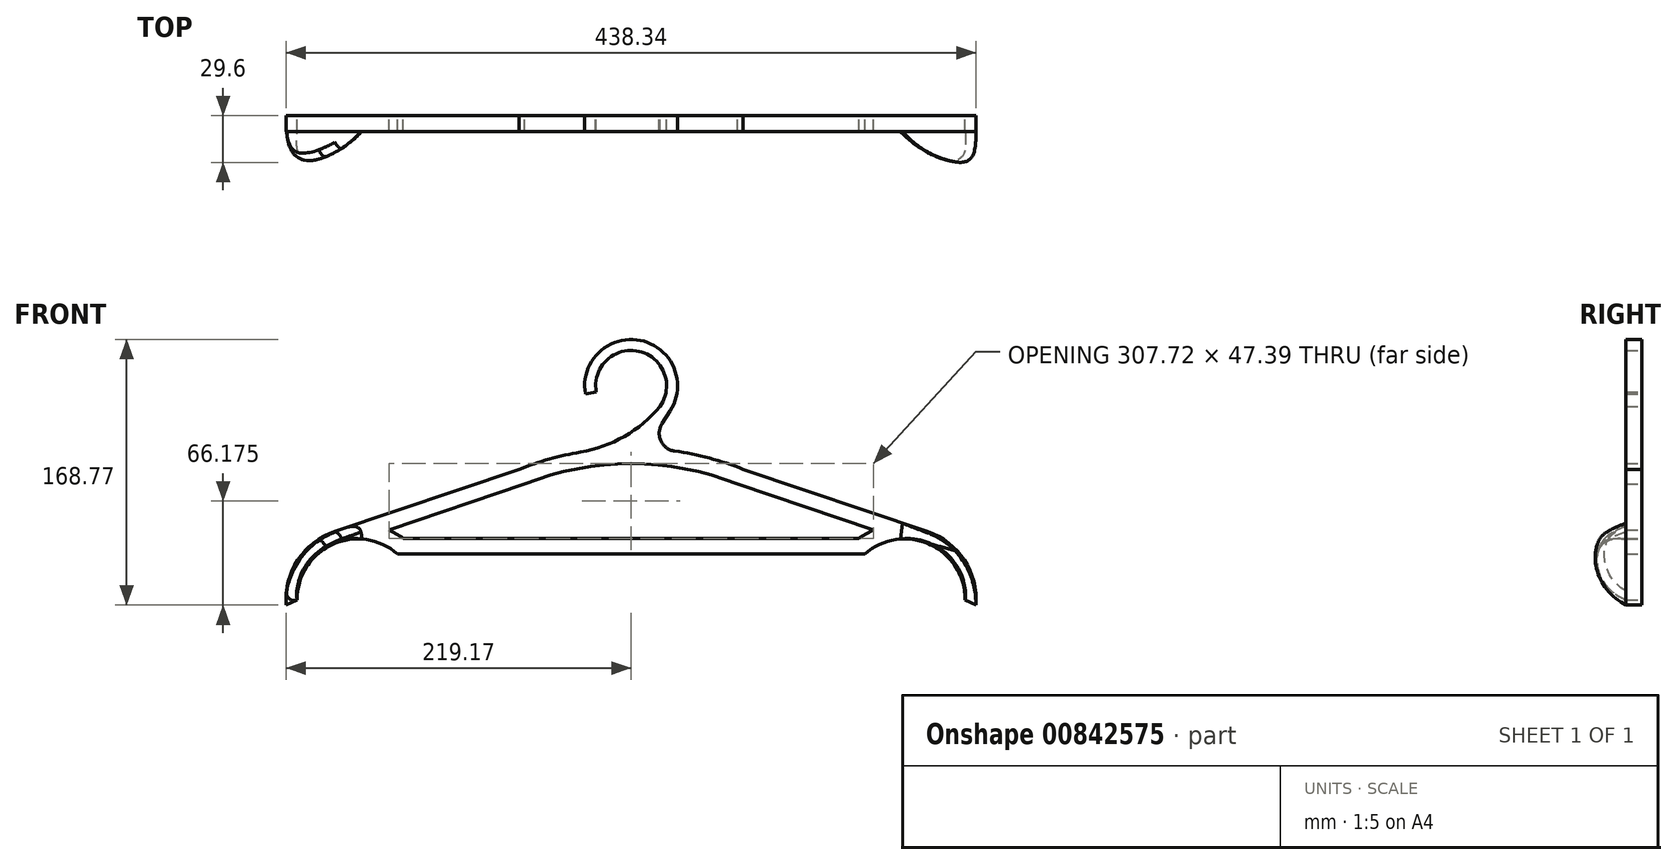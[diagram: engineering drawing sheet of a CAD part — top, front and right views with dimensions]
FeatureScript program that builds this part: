
annotation { "Feature Type Name" : "Feature", "Feature Type Description" : "" }
export const myFeature = defineFeature(function(context is Context, id is Id, definition is map)
    precondition{}
    {
        {
            var Q0;
            Q0=qCreatedBy(makeId("Front.planeOp"),FACE);
            var sketch = newSketch(context, id + "F0", { "sketchPlane" : qUnion([Q0])});
            skLineSegment(sketch, "E0.top", {"start": v(212.5, 102.5) * mm, "end": v(-212.5, 102.5) * mm, "construction": true});
            skPoint(sketch, "E0.middle", {"position": v(0, 0) * mm});
            skLineSegment(sketch, "E1", {"start": v(0, -35.02) * mm, "end": v(0, 25.02) * mm, "construction": true});
            skArc(sketch, "E2", {"start": v(-188.33, -20.83) * mm, "mid": v(-211.7, -38.89) * mm, "end": v(-219.02, -67.5) * mm});
            skArc(sketch, "E3", {"start": v(24.82, 55.82) * mm, "mid": v(5.78, 100.7) * mm, "end": v(-29.04, 66.58) * mm});
            skArc(sketch, "E4.0", {"start": v(15.87, 55.82) * mm, "mid": v(6.77, 93.23) * mm, "end": v(-22.15, 67.81) * mm});
            skArc(sketch, "E5.0", {"start": v(148.4, -35.02) * mm, "mid": v(189.72, -28.9) * mm, "end": v(212.17, -64.13) * mm});
            skArc(sketch, "E6.0", {"start": v(-148.4, -35.02) * mm, "mid": v(-189.72, -28.9) * mm, "end": v(-212.17, -64.13) * mm});
            skLineSegment(sketch, "E7", {"start": v(173.49, -109.23) * mm, "end": v(174.07, -109.23) * mm});
            skLineSegment(sketch, "E8.MirrorCS", {"start": v(71.13, 18.83) * mm, "end": v(188.33, -20.83) * mm});
            skPoint(sketch, "E9.start.orphan", {"position": v(-188.33, -28.3) * mm});
            skPoint(sketch, "E10.orphan", {"position": v(-173.49, -102.23) * mm});
            skLineSegment(sketch, "E11.trimOffspring", {"start": v(173.78, -102.23) * mm, "end": v(174.07, -102.23) * mm});
            skArc(sketch, "E12.trimOffspring", {"start": v(188.33, -20.83) * mm, "mid": v(211.7, -38.89) * mm, "end": v(219.02, -67.5) * mm});
            skPoint(sketch, "E13.MirrorCS.start.orphan", {"position": v(188.33, -28.3) * mm});
            skLineSegment(sketch, "E14.trimOffspring", {"start": v(212.5, -40.14) * mm, "end": v(212.5, 102.5) * mm, "construction": true});
            skPoint(sketch, "E0.bottom.start.orphan", {"position": v(212.5, -102.5) * mm});
            skLineSegment(sketch, "E15", {"start": v(-4.97, 25.02) * mm, "end": v(-4.97, 24.95) * mm, "construction": true});
            skLineSegment(sketch, "E16", {"start": v(5.03, 24.95) * mm, "end": v(5.03, 25.02) * mm, "construction": true});
            skLineSegment(sketch, "E17", {"start": v(9.6, 32.13) * mm, "end": v(24.82, 55.82) * mm});
            skLineSegment(sketch, "E18", {"start": v(0, 32.37) * mm, "end": v(7.33, 43.2) * mm});
            skLineSegment(sketch, "E19", {"start": v(-22.15, 67.81) * mm, "end": v(-29.04, 66.58) * mm});
            skPoint(sketch, "E20.third.point", {"position": v(0, 32.37) * mm});
            skLineSegment(sketch, "E21.trimOffspring", {"start": v(-71.13, 18.83) * mm, "end": v(-188.33, -20.83) * mm});
            skPoint(sketch, "E22.orphan", {"position": v(-52.84, 25.02) * mm});
            skArc(sketch, "E23.trimOffspring", {"start": v(0, 32.37) * mm, "mid": v(-36.2, 28.95) * mm, "end": v(-71.13, 18.83) * mm});
            skPoint(sketch, "E24.orphan", {"position": v(15.87, 55.82) * mm});
            skLineSegment(sketch, "E25", {"start": v(7.33, 43.2) * mm, "end": v(15.87, 55.82) * mm});
            skArc(sketch, "E26.trimOffspring", {"start": v(71.13, 18.83) * mm, "mid": v(40.9, 28) * mm, "end": v(9.6, 32.13) * mm});
            skPoint(sketch, "E27.start.orphan", {"position": v(0, 25.02) * mm});
            skPoint(sketch, "E28.right.start.orphan", {"position": v(-52.84, 17.55) * mm});
            skPoint(sketch, "E29.orphan", {"position": v(52.84, 25.02) * mm});
            skPoint(sketch, "E30.orphan", {"position": v(52.84, 17.55) * mm});
            skLineSegment(sketch, "E31.0", {"start": v(-52.84, -35.02) * mm, "end": v(-138.7, -35.02) * mm});
            skLineSegment(sketch, "E31.1", {"start": v(52.84, -35.02) * mm, "end": v(-52.84, -35.02) * mm});
            skLineSegment(sketch, "E31.2", {"start": v(52.84, -35.02) * mm, "end": v(138.7, -35.02) * mm});
            skLineSegment(sketch, "E32", {"start": v(-138.7, -35.02) * mm, "end": v(-148.4, -35.02) * mm});
            skLineSegment(sketch, "E33", {"start": v(-212.17, -64.13) * mm, "end": v(-219.02, -67.5) * mm});
            skLineSegment(sketch, "E34.MirrorCS", {"start": v(212.17, -64.13) * mm, "end": v(219.02, -67.5) * mm});
            skLineSegment(sketch, "E35.MirrorCS", {"start": v(138.7, -35.02) * mm, "end": v(148.4, -35.02) * mm});
            skPoint(sketch, "E36.orphan", {"position": v(-241.12, -78.36) * mm});
            skPoint(sketch, "E37.orphan", {"position": v(-173.49, -109.23) * mm});
            skPoint(sketch, "E38.orphan", {"position": v(-152.98, -35.02) * mm});
            skArc(sketch, "E39.trimOffspring", {"start": v(174.07, -109.23) * mm, "mid": v(173.78, -109.23) * mm, "end": v(173.49, -109.23) * mm});
            skPoint(sketch, "E40.orphan", {"position": v(152.98, -35.02) * mm});
            skPoint(sketch, "E41.orphan", {"position": v(241.12, -78.36) * mm});
            skPoint(sketch, "E42.orphan", {"position": v(0, -102.5) * mm});
            skPoint(sketch, "E28.top.start.orphan", {"position": v(52.84, -25.02) * mm});
            skPoint(sketch, "E43.trimOffspring.start.orphan", {"position": v(150.24, -25.02) * mm});
            skPoint(sketch, "E44.start.orphan", {"position": v(-52.84, -25.02) * mm});
            skPoint(sketch, "E45.trimOffspring.start.orphan", {"position": v(-150.24, -25.02) * mm});
            skLineSegment(sketch, "E46.trimOffspring", {"start": v(0, 32.37) * mm, "end": v(0, 102.5) * mm, "construction": true});
            skPoint(sketch, "E47.visualSharp", {"position": v(163, -19.73) * mm});
            skPoint(sketch, "E48.visualSharp", {"position": v(-163, -19.73) * mm});
            skLineSegment(sketch, "E49.0", {"start": v(52.84, -25.02) * mm, "end": v(-52.84, -25.02) * mm});
            skLineSegment(sketch, "E49.1", {"start": v(52.84, -25.02) * mm, "end": v(138.7, -25.02) * mm});
            skLineSegment(sketch, "E49.2", {"start": v(138.7, -25.02) * mm, "end": v(144.87, -25.02) * mm});
            skArc(sketch, "E49.3", {"start": v(144.87, -25.02) * mm, "mid": v(149.22, -22.13) * mm, "end": v(153.86, -19.73) * mm});
            skLineSegment(sketch, "E49.4", {"start": v(67.68, 9.44) * mm, "end": v(153.86, -19.73) * mm});
            skLineSegment(sketch, "E49.5", {"start": v(-52.84, -25.02) * mm, "end": v(-138.7, -25.02) * mm});
            skLineSegment(sketch, "E49.6", {"start": v(-138.7, -25.02) * mm, "end": v(-144.87, -25.02) * mm});
            skArc(sketch, "E49.7", {"start": v(-144.87, -25.02) * mm, "mid": v(-149.22, -22.13) * mm, "end": v(-153.86, -19.73) * mm});
            skLineSegment(sketch, "E49.8", {"start": v(-67.68, 9.44) * mm, "end": v(-153.86, -19.73) * mm});
            skArc(sketch, "E49.9", {"start": v(-8.7, 22.16) * mm, "mid": v(-38.72, 18.24) * mm, "end": v(-67.68, 9.44) * mm});
            skArc(sketch, "E49.10", {"start": v(67.68, 9.44) * mm, "mid": v(30.17, 19.87) * mm, "end": v(-8.7, 22.16) * mm});
            skPoint(sketch, "E50.orphan", {"position": v(-212.5, -102.5) * mm});
            skSolve(sketch);
        }
        {
            var Q0;
            {var subQ6=sQuery(id+"F0.wireOp",EDGE,"E2");Q0=makeQuery(id+"F0.imprint","IMPRINT",FACE,{"disambiguationData":[TD([[makeQuery(id+"F0.imprint","IMPRINT",EDGE,{"derivedFrom":subQ6}),1.0]])]});}
            extrude(context, id + "F1", {"entities" : qUnion([Q0]), "depth" : 10 * mm, "offsetDistance" : 25 * mm});
        }
        {
            var Q0;
            Q0=makeQuery(id+"F1.opExtrude","SWEPT_EDGE",EDGE,{"disambiguationData":[OSD([sQuery(id+"F0.wireOp",EDGE,"E4.0"),sQuery(id+"F0.wireOp",EDGE,"E25")])]});
            fillet(context, id + "F2", {"entities" : qUnion([Q0]), "radius" : 1373.13 * mm, "tangentPropagation" : true, "allowEdgeOverflow" : false});
        }
        {
            var Q0;
            Q0=makeQuery(id+"F1.opExtrude","SWEPT_EDGE",EDGE,{"disambiguationData":[OSD([sQuery(id+"F0.wireOp",EDGE,"E17"),sQuery(id+"F0.wireOp",EDGE,"E26.trimOffspring")])]});
            fillet(context, id + "F3", {"entities" : qUnion([Q0]), "radius" : 11.34 * mm, "tangentPropagation" : true, "allowEdgeOverflow" : false});
        }
        {
            var Q0;
            Q0=makeQuery(id+"F2.opFillet","BLEND_EDGE",EDGE,{"blendedFrom":[makeQuery(id+"F1.opExtrude","SWEPT_EDGE",EDGE,{"disambiguationData":[OSD([sQuery(id+"F0.wireOp",EDGE,"E4.0"),sQuery(id+"F0.wireOp",EDGE,"E25")])]}),makeQuery(id+"F1.opExtrude","SWEPT_FACE",FACE,{"disambiguationData":[OSD([sQuery(id+"F0.wireOp",EDGE,"E23.trimOffspring")])]})],"blendedInto":[makeQuery(id+"F1.opExtrude","SWEPT_FACE",FACE,{"disambiguationData":[OSD([sQuery(id+"F0.wireOp",EDGE,"E23.trimOffspring")])]})]});
            fillet(context, id + "F4", {"entities" : qUnion([Q0]), "radius" : 83.47 * mm, "tangentPropagation" : true, "allowEdgeOverflow" : false});
        }
        {
            var Q0;
            Q0=makeQuery(id+"F1.opExtrude","CAP_FACE",FACE,{"disambiguationData":[OSD([sQuery(id+"F0.wireOp",EDGE,"E2"),sQuery(id+"F0.wireOp",EDGE,"E3"),sQuery(id+"F0.wireOp",EDGE,"E4.0"),sQuery(id+"F0.wireOp",EDGE,"E5.0"),sQuery(id+"F0.wireOp",EDGE,"E6.0"),sQuery(id+"F0.wireOp",EDGE,"E8.MirrorCS"),sQuery(id+"F0.wireOp",EDGE,"E12.trimOffspring"),sQuery(id+"F0.wireOp",EDGE,"E17"),sQuery(id+"F0.wireOp",EDGE,"E18"),sQuery(id+"F0.wireOp",EDGE,"E19"),sQuery(id+"F0.wireOp",EDGE,"E21.trimOffspring"),sQuery(id+"F0.wireOp",EDGE,"E23.trimOffspring"),sQuery(id+"F0.wireOp",EDGE,"E25"),sQuery(id+"F0.wireOp",EDGE,"E26.trimOffspring"),sQuery(id+"F0.wireOp",EDGE,"E31.0"),sQuery(id+"F0.wireOp",EDGE,"E31.1"),sQuery(id+"F0.wireOp",EDGE,"E31.2"),sQuery(id+"F0.wireOp",EDGE,"E32"),sQuery(id+"F0.wireOp",EDGE,"E33"),sQuery(id+"F0.wireOp",EDGE,"E34.MirrorCS"),sQuery(id+"F0.wireOp",EDGE,"E35.MirrorCS"),sQuery(id+"F0.wireOp",EDGE,"E49.0"),sQuery(id+"F0.wireOp",EDGE,"E49.1"),sQuery(id+"F0.wireOp",EDGE,"E49.2"),sQuery(id+"F0.wireOp",EDGE,"E49.3"),sQuery(id+"F0.wireOp",EDGE,"E49.4"),sQuery(id+"F0.wireOp",EDGE,"E49.5"),sQuery(id+"F0.wireOp",EDGE,"E49.6"),sQuery(id+"F0.wireOp",EDGE,"E49.7"),sQuery(id+"F0.wireOp",EDGE,"E49.8"),sQuery(id+"F0.wireOp",EDGE,"E49.9"),sQuery(id+"F0.wireOp",EDGE,"E49.10")])],"isStart":false});
            var sketch = newSketch(context, id + "F5", { "sketchPlane" : qUnion([Q0])});
            skLineSegment(sketch, "E51", {"start": v(0, 0) * mm, "end": v(0, 30.4) * mm, "construction": true});
            skPoint(sketch, "E52", {"position": v(-172.44, -15.46) * mm});
            skLineSegment(sketch, "E53", {"start": v(-172.44, -15.46) * mm, "end": v(-171.03, -25.54) * mm});
            skLineSegment(sketch, "E54", {"start": v(172.44, -15.46) * mm, "end": v(171.03, -25.54) * mm});
            skPoint(sketch, "E55.MirrorCS.start.orphan", {"position": v(153.86, -19.73) * mm});
            skPoint(sketch, "E56.center.orphan", {"position": v(-173.78, -63.83) * mm});
            skPoint(sketch, "E56.start.orphan", {"position": v(-153.86, -19.73) * mm});
            skSolve(sketch);
        }
        {
            var Q0;
            {var subQ2=sQuery(id+"F5.wireOp",EDGE,"E53");Q0=makeQuery(id+"F5.imprint","IMPRINT",FACE,{"disambiguationData":[TD([[makeQuery(id+"F5.imprint","IMPRINT",EDGE,{"derivedFrom":subQ2}),-1.0]])]});}
            var Q1;
            {var subQ2=sQuery(id+"F5.wireOp",EDGE,"E54");Q1=makeQuery(id+"F5.imprint","IMPRINT",FACE,{"disambiguationData":[TD([[makeQuery(id+"F5.imprint","IMPRINT",EDGE,{"derivedFrom":subQ2}),1.0]])]});}
            extrude(context, id + "F6", {"entities" : qUnion([Q0, Q1]), "depth" : 20 * mm, "offsetDistance" : 25 * mm, "hasDraft" : true, "draftAngle" : 3 * degree, "draftPullDirection" : true});
        }
        {
            var Q0;
            Q0=makeQuery(id+"F6.opExtrude","CAP_EDGE",EDGE,{"disambiguationData":[OSD([sQuery(id+"F5.wireOp",EDGE,"E54")])],"isStart":false});
            var Q1;
            Q1=makeQuery(id+"F6.opExtrude","CAP_EDGE",EDGE,{"disambiguationData":[OSD([sQuery(id+"F5.wireOp",EDGE,"E53")])],"isStart":false});
            fillet(context, id + "F7", {"entities" : qUnion([Q0, Q1]), "radius" : 60 * mm, "tangentPropagation" : true, "allowEdgeOverflow" : false});
        }
        {
            var Q0;
            Q0=makeQuery(id+"F6.opExtrude","CAP_EDGE",EDGE,{"disambiguationData":[OSD([sQuery(id+"F0.wireOp",EDGE,"E34.MirrorCS")])],"isStart":false});
            var Q1;
            Q1=makeQuery(id+"F6.opExtrude","CAP_EDGE",EDGE,{"disambiguationData":[OSD([sQuery(id+"F0.wireOp",EDGE,"E33")])],"isStart":false});
            fillet(context, id + "F8", {"entities" : qUnion([Q0, Q1]), "radius" : 27.73 * mm, "tangentPropagation" : true, "allowEdgeOverflow" : false});
        }
        {
            var Q0;
            Q0=makeQuery(id+"F7.opFillet","BLEND_EDGE",EDGE,{"blendedFrom":[makeQuery(id+"F6.opExtrude","CAP_EDGE",EDGE,{"disambiguationData":[OSD([sQuery(id+"F5.wireOp",EDGE,"E53")])],"isStart":false}),makeQuery(id+"F6.opExtrude","SWEPT_FACE",FACE,{"disambiguationData":[OSD([sQuery(id+"F0.wireOp",EDGE,"E21.trimOffspring")])]})],"blendedInto":[makeQuery(id+"F6.opExtrude","SWEPT_FACE",FACE,{"disambiguationData":[OSD([sQuery(id+"F0.wireOp",EDGE,"E21.trimOffspring")])]})]});
            fillet(context, id + "F9", {"entities" : qUnion([Q0]), "radius" : 5 * mm, "tangentPropagation" : true, "allowEdgeOverflow" : false});
        }
    });
